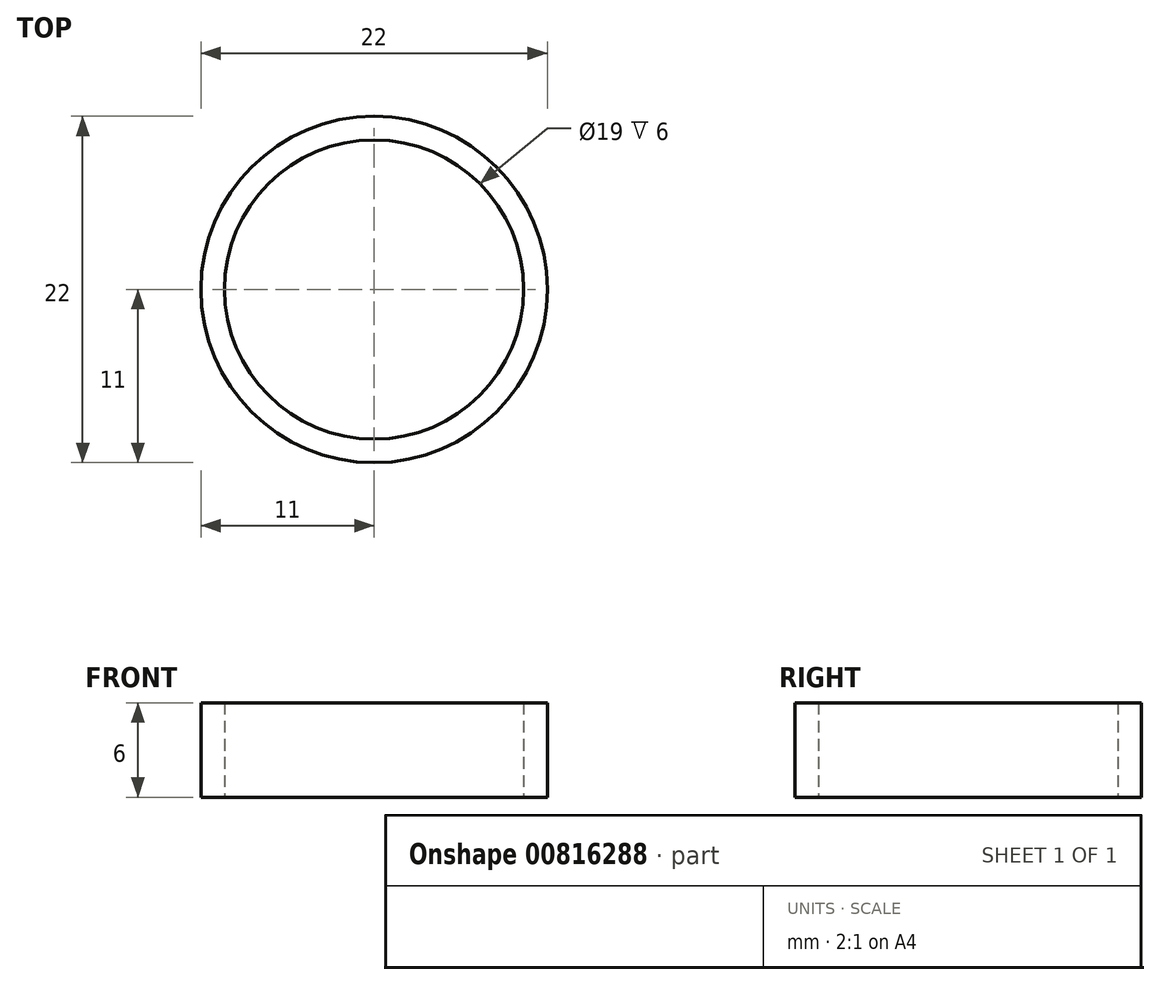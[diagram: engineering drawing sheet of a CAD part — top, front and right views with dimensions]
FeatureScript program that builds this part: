
annotation { "Feature Type Name" : "Feature", "Feature Type Description" : "" }
export const myFeature = defineFeature(function(context is Context, id is Id, definition is map)
    precondition{}
    {
        {
            var Q0;
            Q0=qCreatedBy(makeId("Top.planeOp"),FACE);
            var sketch = newSketch(context, id + "F0", { "sketchPlane" : qUnion([Q0])});
            skCircle(sketch, "E0", {"center": v(0, 0) * mm, "radius": 11 * mm});
            skCircle(sketch, "E1", {"center": v(0, 0) * mm, "radius": 9.5 * mm});
            skSolve(sketch);
        }
        {
            var Q0;
            Q0=makeQuery(id+"F0.imprint","IMPRINT",FACE,{"disambiguationData":[TD([[makeQuery(id+"F0.imprint","IMPRINT",EDGE,{"derivedFrom":sQuery(id+"F0.wireOp",EDGE,"E0")}),1.0]])]});
            extrude(context, id + "F1", {"entities" : qUnion([Q0]), "depth" : 6 * mm, "offsetDistance" : 25 * mm});
        }
    });
